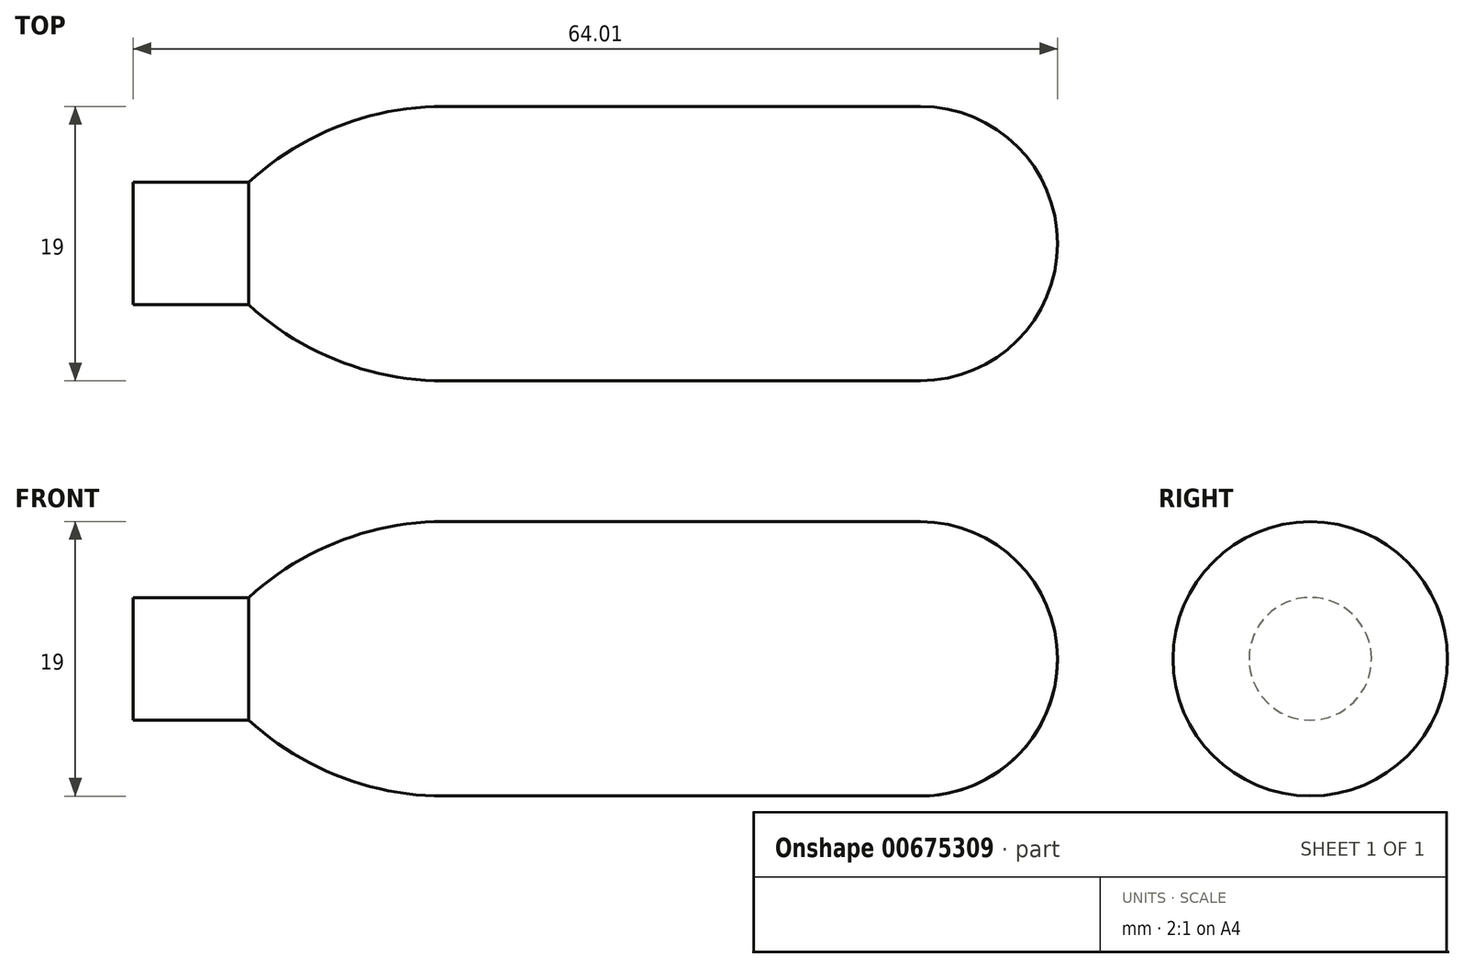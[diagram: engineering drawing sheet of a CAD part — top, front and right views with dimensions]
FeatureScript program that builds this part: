
annotation { "Feature Type Name" : "Feature", "Feature Type Description" : "" }
export const myFeature = defineFeature(function(context is Context, id is Id, definition is map)
    precondition{}
    {
        {
            var Q0;
            Q0=qCreatedBy(makeId("Front.planeOp"),FACE);
            var sketch = newSketch(context, id + "F0", { "sketchPlane" : qUnion([Q0])});
            skLineSegment(sketch, "E0", {"start": v(0, 0) * mm, "end": v(0, 4.24) * mm});
            skLineSegment(sketch, "E1", {"start": v(0, 4.24) * mm, "end": v(8, 4.24) * mm});
            skLineSegment(sketch, "E2", {"start": v(21.51, 9.5) * mm, "end": v(54.5, 9.5) * mm});
            skLineSegment(sketch, "E3", {"start": v(64, 0) * mm, "end": v(0, 0) * mm});
            skArc(sketch, "E4", {"start": v(64, 0) * mm, "mid": v(61.23, 6.72) * mm, "end": v(54.5, 9.5) * mm});
            skArc(sketch, "E5", {"start": v(21.51, 9.5) * mm, "mid": v(14.26, 8.14) * mm, "end": v(8, 4.24) * mm});
            skSolve(sketch);
        }
        {
            var Q0;
            Q0=makeQuery(id+"F0.imprint","IMPRINT",FACE,{"disambiguationData":[TD([[makeQuery(id+"F0.imprint","IMPRINT",EDGE,{"derivedFrom":sQuery(id+"F0.wireOp",EDGE,"E0")}),-1.0]])]});
            var Q1;
            Q1=sQuery(id+"F0.wireOp",EDGE,"E3");
            revolve(context, id + "F1", {"entities" : qUnion([Q0]), "axis" : qUnion([Q1]), "revolveType" : RevolveType.FULL});
        }
    });
